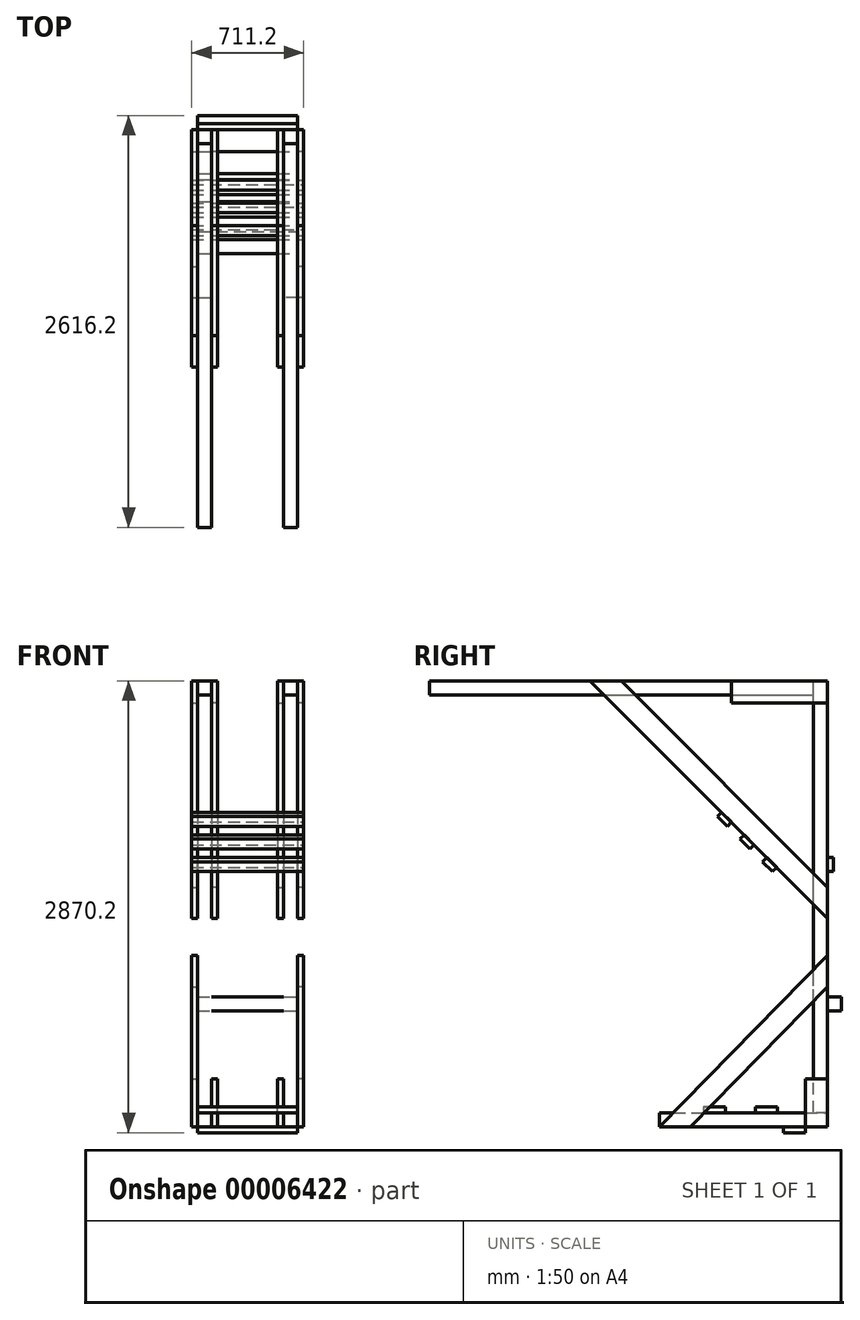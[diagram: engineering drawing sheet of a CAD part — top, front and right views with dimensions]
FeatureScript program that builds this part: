
annotation { "Feature Type Name" : "Feature", "Feature Type Description" : "" }
export const myFeature = defineFeature(function(context is Context, id is Id, definition is map)
    precondition{}
    {
        {
            var Q0;
            Q0=qCreatedBy(makeId("Top.planeOp"),FACE);
            var sketch = newSketch(context, id + "F0", { "sketchPlane" : qUnion([Q0])});
            skLineSegment(sketch, "E0.bottom", {"start": v(-317.5, 0) * mm, "end": v(-228.6, 0) * mm});
            skLineSegment(sketch, "E0.top", {"start": v(-317.5, -88.9) * mm, "end": v(-228.6, -88.9) * mm});
            skLineSegment(sketch, "E0.left", {"start": v(-317.5, 0) * mm, "end": v(-317.5, -88.9) * mm});
            skLineSegment(sketch, "E0.right", {"start": v(-228.6, 0) * mm, "end": v(-228.6, -88.9) * mm});
            skSolve(sketch);
        }
        {
            var Q0;
            Q0 = qSketchRegion(id + "F0", true);
            extrude(context, id + "F1", {"entities" : qUnion([Q0]), "oppositeDirection" : true, "depth" : 2743.2 * mm});
        }
        {
            var Q0;
            Q0=makeQuery(id+"F1.opExtrude","SWEPT_FACE",FACE,{"disambiguationData":[OSD([sQuery(id+"F0.wireOp",EDGE,"E0.bottom")])]});
            var sketch = newSketch(context, id + "F2", { "sketchPlane" : qUnion([Q0])});
            skLineSegment(sketch, "E1.bottom", {"start": v(317.5, -2832.1) * mm, "end": v(228.6, -2832.1) * mm});
            skLineSegment(sketch, "E1.top", {"start": v(317.5, -2743.2) * mm, "end": v(228.6, -2743.2) * mm});
            skLineSegment(sketch, "E1.left", {"start": v(228.6, -2832.1) * mm, "end": v(228.6, -2743.2) * mm});
            skLineSegment(sketch, "E1.right", {"start": v(317.5, -2832.1) * mm, "end": v(317.5, -2743.2) * mm});
            skSolve(sketch);
        }
        {
            var Q0;
            Q0=makeQuery(id+"F2.imprint","IMPRINT",FACE,{"disambiguationData":[TD([[makeQuery(id+"F2.imprint","IMPRINT",EDGE,{"derivedFrom":sQuery(id+"F2.wireOp",EDGE,"E1.bottom")}),-1.0]])]});
            extrude(context, id + "F3", {"entities" : qUnion([Q0]), "oppositeDirection" : true, "depth" : 1066.8 * mm});
        }
        {
            var Q0;
            Q0=makeQuery(id+"F1.opExtrude","SWEPT_FACE",FACE,{"disambiguationData":[OSD([sQuery(id+"F0.wireOp",EDGE,"E0.right")])]});
            var sketch = newSketch(context, id + "F4", { "sketchPlane" : qUnion([Q0])});
            skLineSegment(sketch, "E2.bottom", {"start": v(0, -2832.1) * mm, "end": v(-139.7, -2832.1) * mm});
            skLineSegment(sketch, "E2.top", {"start": v(0, -2527.3) * mm, "end": v(-139.7, -2527.3) * mm});
            skLineSegment(sketch, "E2.left", {"start": v(0, -2832.1) * mm, "end": v(0, -2527.3) * mm});
            skLineSegment(sketch, "E2.right", {"start": v(-139.7, -2832.1) * mm, "end": v(-139.7, -2527.3) * mm});
            skSolve(sketch);
        }
        {
            var Q0;
            {var subQ5=sQuery(id+"F4.wireOp",EDGE,"E2.right");Q0=makeQuery(id+"F4.imprint","IMPRINT",FACE,{"disambiguationData":[TD([[makeQuery(id+"F4.imprint","IMPRINT",EDGE,{"derivedFrom":subQ5}),-1.0]])]});}
            var Q1;
            {var subQ6=sQuery(id+"F4.wireOp",EDGE,"E2.left");Q1=makeQuery(id+"F4.imprint","IMPRINT",FACE,{"disambiguationData":[TD([[makeQuery(id+"F4.imprint","IMPRINT",EDGE,{"derivedFrom":subQ6}),1.0]])]});}
            extrude(context, id + "F5", {"entities" : qUnion([Q0, Q1]), "depth" : 38.1 * mm});
        }
        {
            var Q0;
            Q0=makeQuery(id+"F1.opExtrude","SWEPT_FACE",FACE,{"disambiguationData":[OSD([sQuery(id+"F0.wireOp",EDGE,"E0.top")])]});
            var sketch = newSketch(context, id + "F6", { "sketchPlane" : qUnion([Q0])});
            skLineSegment(sketch, "E3.bottom", {"start": v(-317.5, 0) * mm, "end": v(-228.6, 0) * mm});
            skLineSegment(sketch, "E3.top", {"start": v(-317.5, -88.9) * mm, "end": v(-228.6, -88.9) * mm});
            skLineSegment(sketch, "E3.left", {"start": v(-317.5, 0) * mm, "end": v(-317.5, -88.9) * mm});
            skLineSegment(sketch, "E3.right", {"start": v(-228.6, 0) * mm, "end": v(-228.6, -88.9) * mm});
            skSolve(sketch);
        }
        {
            var Q0;
            Q0=makeQuery(id+"F6.imprint","IMPRINT",FACE,{"disambiguationData":[TD([[makeQuery(id+"F6.imprint","IMPRINT",EDGE,{"derivedFrom":sQuery(id+"F6.wireOp",EDGE,"E3.bottom")}),-1.0]])]});
            extrude(context, id + "F7", {"entities" : qUnion([Q0]), "depth" : 2438.4 * mm});
        }
        {
            var Q0;
            Q0=makeQuery(id+"F1.opExtrude","SWEPT_FACE",FACE,{"disambiguationData":[OSD([sQuery(id+"F0.wireOp",EDGE,"E0.right")])]});
            var sketch = newSketch(context, id + "F8", { "sketchPlane" : qUnion([Q0])});
            skLineSegment(sketch, "E4.bottom", {"start": v(0, 0) * mm, "end": v(-609.6, 0) * mm});
            skLineSegment(sketch, "E4.top", {"start": v(0, -139.7) * mm, "end": v(-609.6, -139.7) * mm});
            skLineSegment(sketch, "E4.left", {"start": v(0, 0) * mm, "end": v(0, -139.7) * mm});
            skLineSegment(sketch, "E4.right", {"start": v(-609.6, 0) * mm, "end": v(-609.6, -139.7) * mm});
            skLineSegment(sketch, "E5.0", {"start": v(-2527.3, -88.9) * mm, "end": v(-88.9, -88.9) * mm, "construction": true});
            skSolve(sketch);
        }
        {
            var Q0;
            {var subQ5=sQuery(id+"F8.wireOp",EDGE,"E4.right");Q0=makeQuery(id+"F8.imprint","IMPRINT",FACE,{"disambiguationData":[TD([[makeQuery(id+"F8.imprint","IMPRINT",EDGE,{"derivedFrom":subQ5}),1.0]])]});}
            var Q1;
            {var subQ6=sQuery(id+"F8.wireOp",EDGE,"E4.left");Q1=makeQuery(id+"F8.imprint","IMPRINT",FACE,{"disambiguationData":[TD([[makeQuery(id+"F8.imprint","IMPRINT",EDGE,{"derivedFrom":subQ6}),1.0]])]});}
            extrude(context, id + "F9", {"entities" : qUnion([Q0, Q1]), "depth" : 38.1 * mm});
        }
        {
            var Q0;
            Q0=makeQuery(id+"F7.opExtrude","SWEPT_FACE",FACE,{"disambiguationData":[OSD([sQuery(id+"F6.wireOp",EDGE,"E3.right")])]});
            var sketch = newSketch(context, id + "F10", { "sketchPlane" : qUnion([Q0])});
            skLineSegment(sketch, "E6.0", {"start": v(0, -2743.2) * mm, "end": v(0, 0) * mm, "construction": true});
            skLineSegment(sketch, "E7", {"start": v(-1508.68, 0) * mm, "end": v(0, -1508.68) * mm});
            skLineSegment(sketch, "E8", {"start": v(0, -1508.68) * mm, "end": v(0, -1311.12) * mm});
            skLineSegment(sketch, "E9", {"start": v(0, -1311.12) * mm, "end": v(-1311.12, 0) * mm});
            skLineSegment(sketch, "E10", {"start": v(-1311.12, 0) * mm, "end": v(-1508.68, 0) * mm});
            skLineSegment(sketch, "E11", {"start": v(-1311.12, 0) * mm, "end": v(0, 0) * mm, "construction": true});
            skLineSegment(sketch, "E12", {"start": v(0, -1311.12) * mm, "end": v(0, 0) * mm, "construction": true});
            skSolve(sketch);
        }
        {
            var Q0;
            Q0=makeQuery(id+"F7.opExtrude","SWEPT_FACE",FACE,{"disambiguationData":[OSD([sQuery(id+"F6.wireOp",EDGE,"E3.right")])]});
            var Q1;
            Q1=makeQuery(id+"F7.opExtrude","SWEPT_FACE",FACE,{"disambiguationData":[OSD([sQuery(id+"F6.wireOp",EDGE,"E3.left")])]});
            cPlane(context, id + "F11", {"entities" : qUnion([Q0, Q1]), "cplaneType" : CPlaneType.MID_PLANE, "offset" : 152.4 * mm, "width" : 152.4 * mm, "height" : 152.4 * mm});
        }
        {
            var Q0;
            {var subQ5=sQuery(id+"F10.wireOp",EDGE,"E8");Q0=makeQuery(id+"F10.imprint","IMPRINT",FACE,{"disambiguationData":[TD([[makeQuery(id+"F10.imprint","IMPRINT",EDGE,{"derivedFrom":subQ5}),1.0]])]});}
            var Q1;
            {var subQ6=sQuery(id+"F10.wireOp",EDGE,"E10");Q1=makeQuery(id+"F10.imprint","IMPRINT",FACE,{"disambiguationData":[TD([[makeQuery(id+"F10.imprint","IMPRINT",EDGE,{"derivedFrom":subQ6}),-1.0]])]});}
            extrude(context, id + "F12", {"entities" : qUnion([Q0, Q1]), "depth" : 38.1 * mm});
        }
        {
            var Q0;
            Q0=makeQuery(id+"F9.opExtrude","SWEPT_BODY",BODY,{"disambiguationData":[OSD([sQuery(id+"F8.wireOp",EDGE,"E4.bottom"),sQuery(id+"F8.wireOp",EDGE,"E4.top"),sQuery(id+"F8.wireOp",EDGE,"E4.left"),sQuery(id+"F8.wireOp",EDGE,"E4.right")])]});
            var Q1;
            Q1=makeQuery(id+"F5.opExtrude","SWEPT_BODY",BODY,{"disambiguationData":[OSD([sQuery(id+"F4.wireOp",EDGE,"E2.bottom"),sQuery(id+"F4.wireOp",EDGE,"E2.top"),sQuery(id+"F4.wireOp",EDGE,"E2.left"),sQuery(id+"F4.wireOp",EDGE,"E2.right")])]});
            var Q2;
            Q2=makeQuery(id+"F12.opExtrude","SWEPT_BODY",BODY,{"disambiguationData":[OSD([sQuery(id+"F10.wireOp",EDGE,"E7"),sQuery(id+"F10.wireOp",EDGE,"E8"),sQuery(id+"F10.wireOp",EDGE,"E9"),sQuery(id+"F10.wireOp",EDGE,"E10")])]});
            var Q3;
            Q3=qCreatedBy(id+"F11.planeOp",FACE);
            mirror(context, id + "F13", {"entities" : qUnion([Q0, Q1, Q2]), "mirrorPlane" : qUnion([Q3])});
        }
        {
            var Q0;
            Q0=makeQuery(id+"F1.opExtrude","SWEPT_FACE",FACE,{"disambiguationData":[OSD([sQuery(id+"F0.wireOp",EDGE,"E0.left")])]});
            var sketch = newSketch(context, id + "F14", { "sketchPlane" : qUnion([Q0])});
            skLineSegment(sketch, "E13.0", {"start": v(1066.8, -2832.1) * mm, "end": v(0, -2832.1) * mm, "construction": true});
            skLineSegment(sketch, "E14", {"start": v(0, -1943.32) * mm, "end": v(871.18, -2832.1) * mm});
            skLineSegment(sketch, "E15", {"start": v(871.18, -2832.1) * mm, "end": v(1066.8, -2832.1) * mm});
            skLineSegment(sketch, "E16", {"start": v(1066.8, -2832.1) * mm, "end": v(0, -1743.75) * mm});
            skLineSegment(sketch, "E17", {"start": v(0, -1743.75) * mm, "end": v(0, -1943.32) * mm});
            skSolve(sketch);
        }
        {
            var Q0;
            {var subQ5=sQuery(id+"F14.wireOp",EDGE,"E15");Q0=makeQuery(id+"F14.imprint","IMPRINT",FACE,{"disambiguationData":[TD([[makeQuery(id+"F14.imprint","IMPRINT",EDGE,{"derivedFrom":subQ5}),1.0]])]});}
            var Q1;
            {var subQ6=sQuery(id+"F14.wireOp",EDGE,"E17");Q1=makeQuery(id+"F14.imprint","IMPRINT",FACE,{"disambiguationData":[TD([[makeQuery(id+"F14.imprint","IMPRINT",EDGE,{"derivedFrom":subQ6}),-1.0]])]});}
            extrude(context, id + "F15", {"entities" : qUnion([Q0, Q1]), "depth" : 38.1 * mm});
        }
        {
            var Q0;
            Q0=makeQuery(id+"F1.opExtrude","SWEPT_BODY",BODY,{"disambiguationData":[OSD([sQuery(id+"F0.wireOp",EDGE,"E0.bottom"),sQuery(id+"F0.wireOp",EDGE,"E0.top"),sQuery(id+"F0.wireOp",EDGE,"E0.left"),sQuery(id+"F0.wireOp",EDGE,"E0.right")])]});
            var Q1;
            Q1=makeQuery(id+"F3.opExtrude","SWEPT_BODY",BODY,{"disambiguationData":[OSD([sQuery(id+"F2.wireOp",EDGE,"E1.bottom"),sQuery(id+"F2.wireOp",EDGE,"E1.top"),sQuery(id+"F2.wireOp",EDGE,"E1.left"),sQuery(id+"F2.wireOp",EDGE,"E1.right")])]});
            var Q2;
            Q2=makeQuery(id+"F5.opExtrude","SWEPT_BODY",BODY,{"disambiguationData":[OSD([sQuery(id+"F4.wireOp",EDGE,"E2.bottom"),sQuery(id+"F4.wireOp",EDGE,"E2.top"),sQuery(id+"F4.wireOp",EDGE,"E2.left"),sQuery(id+"F4.wireOp",EDGE,"E2.right")])]});
            var Q3;
            Q3=makeQuery(id+"F7.opExtrude","SWEPT_BODY",BODY,{"disambiguationData":[OSD([sQuery(id+"F6.wireOp",EDGE,"E3.bottom"),sQuery(id+"F6.wireOp",EDGE,"E3.top"),sQuery(id+"F6.wireOp",EDGE,"E3.left"),sQuery(id+"F6.wireOp",EDGE,"E3.right")])]});
            var Q4;
            Q4=makeQuery(id+"F9.opExtrude","SWEPT_BODY",BODY,{"disambiguationData":[OSD([sQuery(id+"F8.wireOp",EDGE,"E4.bottom"),sQuery(id+"F8.wireOp",EDGE,"E4.top"),sQuery(id+"F8.wireOp",EDGE,"E4.left"),sQuery(id+"F8.wireOp",EDGE,"E4.right")])]});
            var Q5;
            Q5=makeQuery(id+"F13.opPattern","COPY",BODY,{"derivedFrom":makeQuery(id+"F9.opExtrude","SWEPT_BODY",BODY,{"disambiguationData":[OSD([sQuery(id+"F8.wireOp",EDGE,"E4.bottom"),sQuery(id+"F8.wireOp",EDGE,"E4.top"),sQuery(id+"F8.wireOp",EDGE,"E4.left"),sQuery(id+"F8.wireOp",EDGE,"E4.right")])]}),"instanceName":"1"});
            var Q6;
            Q6=makeQuery(id+"F13.opPattern","COPY",BODY,{"derivedFrom":makeQuery(id+"F5.opExtrude","SWEPT_BODY",BODY,{"disambiguationData":[OSD([sQuery(id+"F4.wireOp",EDGE,"E2.bottom"),sQuery(id+"F4.wireOp",EDGE,"E2.top"),sQuery(id+"F4.wireOp",EDGE,"E2.left"),sQuery(id+"F4.wireOp",EDGE,"E2.right")])]}),"instanceName":"1"});
            var Q7;
            Q7=makeQuery(id+"F15.opExtrude","SWEPT_BODY",BODY,{"disambiguationData":[OSD([sQuery(id+"F14.wireOp",EDGE,"E14"),sQuery(id+"F14.wireOp",EDGE,"E15"),sQuery(id+"F14.wireOp",EDGE,"E16"),sQuery(id+"F14.wireOp",EDGE,"E17")])]});
            var Q8;
            Q8=makeQuery(id+"F13.opPattern","COPY",BODY,{"derivedFrom":makeQuery(id+"F12.opExtrude","SWEPT_BODY",BODY,{"disambiguationData":[OSD([sQuery(id+"F10.wireOp",EDGE,"E7"),sQuery(id+"F10.wireOp",EDGE,"E8"),sQuery(id+"F10.wireOp",EDGE,"E9"),sQuery(id+"F10.wireOp",EDGE,"E10")])]}),"instanceName":"1"});
            var Q9;
            Q9=makeQuery(id+"F12.opExtrude","SWEPT_BODY",BODY,{"disambiguationData":[OSD([sQuery(id+"F10.wireOp",EDGE,"E7"),sQuery(id+"F10.wireOp",EDGE,"E8"),sQuery(id+"F10.wireOp",EDGE,"E9"),sQuery(id+"F10.wireOp",EDGE,"E10")])]});
            var Q10;
            Q10=qCreatedBy(makeId("Right.planeOp"),FACE);
            mirror(context, id + "F16", {"entities" : qUnion([Q0, Q1, Q2, Q3, Q4, Q5, Q6, Q7, Q8, Q9]), "mirrorPlane" : qUnion([Q10])});
        }
        {
            var Q0;
            Q0=makeQuery(id+"F3.opExtrude","SWEPT_FACE",FACE,{"disambiguationData":[OSD([sQuery(id+"F2.wireOp",EDGE,"E1.top")])]});
            var sketch = newSketch(context, id + "F17", { "sketchPlane" : qUnion([Q0])});
            skLineSegment(sketch, "E18.bottom", {"start": v(-317.5, -317.5) * mm, "end": v(317.5, -317.5) * mm});
            skLineSegment(sketch, "E18.top", {"start": v(-317.5, -457.2) * mm, "end": v(317.5, -457.2) * mm});
            skLineSegment(sketch, "E18.left", {"start": v(-317.5, -317.5) * mm, "end": v(-317.5, -457.2) * mm});
            skLineSegment(sketch, "E18.right", {"start": v(317.5, -317.5) * mm, "end": v(317.5, -457.2) * mm});
            skLineSegment(sketch, "E19.bottom", {"start": v(-317.5, -647.7) * mm, "end": v(317.5, -647.7) * mm});
            skLineSegment(sketch, "E19.top", {"start": v(-317.5, -787.4) * mm, "end": v(317.5, -787.4) * mm});
            skLineSegment(sketch, "E19.left", {"start": v(-317.5, -647.7) * mm, "end": v(-317.5, -787.4) * mm});
            skLineSegment(sketch, "E19.right", {"start": v(317.5, -647.7) * mm, "end": v(317.5, -787.4) * mm});
            skSolve(sketch);
        }
        {
            var Q0;
            Q0 = qSketchRegion(id + "F17", true);
            extrude(context, id + "F18", {"entities" : qUnion([Q0]), "depth" : 38.1 * mm});
        }
        {
            var Q0;
            Q0=makeQuery(id+"F3.opExtrude","SWEPT_FACE",FACE,{"disambiguationData":[OSD([sQuery(id+"F2.wireOp",EDGE,"E1.bottom")])]});
            var sketch = newSketch(context, id + "F19", { "sketchPlane" : qUnion([Q0])});
            skLineSegment(sketch, "E20.bottom", {"start": v(-317.5, 139.7) * mm, "end": v(317.5, 139.7) * mm});
            skLineSegment(sketch, "E20.top", {"start": v(-317.5, 279.4) * mm, "end": v(317.5, 279.4) * mm});
            skLineSegment(sketch, "E20.left", {"start": v(-317.5, 139.7) * mm, "end": v(-317.5, 279.4) * mm});
            skLineSegment(sketch, "E20.right", {"start": v(317.5, 139.7) * mm, "end": v(317.5, 279.4) * mm});
            skSolve(sketch);
        }
        {
            var Q0;
            Q0 = qSketchRegion(id + "F19", true);
            extrude(context, id + "F20", {"entities" : qUnion([Q0]), "depth" : 38.1 * mm});
        }
        {
            var Q0;
            Q0=makeQuery(id+"F1.opExtrude","SWEPT_FACE",FACE,{"disambiguationData":[OSD([sQuery(id+"F0.wireOp",EDGE,"E0.bottom")])]});
            var sketch = newSketch(context, id + "F21", { "sketchPlane" : qUnion([Q0])});
            skLineSegment(sketch, "E21.bottom", {"start": v(317.5, -2006.6) * mm, "end": v(-317.5, -2006.6) * mm});
            skLineSegment(sketch, "E21.top", {"start": v(317.5, -2095.5) * mm, "end": v(-317.5, -2095.5) * mm});
            skLineSegment(sketch, "E21.left", {"start": v(317.5, -2006.6) * mm, "end": v(317.5, -2095.5) * mm});
            skLineSegment(sketch, "E21.right", {"start": v(-317.5, -2006.6) * mm, "end": v(-317.5, -2095.5) * mm});
            skSolve(sketch);
        }
        {
            var Q0;
            Q0 = qSketchRegion(id + "F21", true);
            extrude(context, id + "F22", {"entities" : qUnion([Q0]), "depth" : 88.9 * mm});
        }
        {
            var Q0;
            Q0=makeQuery(id+"F13.opPattern","COPY",FACE,{"derivedFrom":makeQuery(id+"F12.opExtrude","SWEPT_FACE",FACE,{"disambiguationData":[OSD([sQuery(id+"F10.wireOp",EDGE,"E7")])]}),"instanceName":"1"});
            var sketch = newSketch(context, id + "F23", { "sketchPlane" : qUnion([Q0])});
            skLineSegment(sketch, "E22.bottom", {"start": v(-355.6, -609.6) * mm, "end": v(355.6, -609.6) * mm});
            skLineSegment(sketch, "E22.top", {"start": v(-355.6, -520.7) * mm, "end": v(355.6, -520.7) * mm});
            skLineSegment(sketch, "E22.left", {"start": v(-355.6, -609.6) * mm, "end": v(-355.6, -520.7) * mm});
            skLineSegment(sketch, "E22.right", {"start": v(355.6, -609.6) * mm, "end": v(355.6, -520.7) * mm});
            skLineSegment(sketch, "E23.0.1.0", {"start": v(-355.6, -406.4) * mm, "end": v(355.6, -406.4) * mm});
            skLineSegment(sketch, "E23.0.1.1", {"start": v(-355.6, -317.5) * mm, "end": v(355.6, -317.5) * mm});
            skLineSegment(sketch, "E23.0.1.2", {"start": v(355.6, -406.4) * mm, "end": v(355.6, -317.5) * mm});
            skLineSegment(sketch, "E23.0.1.3", {"start": v(-355.6, -406.4) * mm, "end": v(-355.6, -317.5) * mm});
            skLineSegment(sketch, "E23.0.2.0", {"start": v(-355.6, -203.2) * mm, "end": v(355.6, -203.2) * mm});
            skLineSegment(sketch, "E23.0.2.1", {"start": v(-355.6, -114.3) * mm, "end": v(355.6, -114.3) * mm});
            skLineSegment(sketch, "E23.0.2.2", {"start": v(355.6, -203.2) * mm, "end": v(355.6, -114.3) * mm});
            skLineSegment(sketch, "E23.0.2.3", {"start": v(-355.6, -203.2) * mm, "end": v(-355.6, -114.3) * mm});
            skLineSegment(sketch, "E23.direction1", {"start": v(-355.6, -609.6) * mm, "end": v(-330.2, -609.6) * mm, "construction": true});
            skLineSegment(sketch, "E23.direction2", {"start": v(-355.6, -609.6) * mm, "end": v(-355.6, -406.4) * mm, "construction": true});
            skSolve(sketch);
        }
        {
            var Q0;
            Q0 = qSketchRegion(id + "F23", true);
            extrude(context, id + "F24", {"entities" : qUnion([Q0]), "depth" : 38.1 * mm});
        }
        {
            var Q0;
            Q0=makeQuery(id+"F1.opExtrude","SWEPT_FACE",FACE,{"disambiguationData":[OSD([sQuery(id+"F0.wireOp",EDGE,"E0.bottom")])]});
            var sketch = newSketch(context, id + "F25", { "sketchPlane" : qUnion([Q0])});
            skLineSegment(sketch, "E24.bottom", {"start": v(317.5, -1212.33) * mm, "end": v(-317.5, -1212.33) * mm});
            skLineSegment(sketch, "E24.top", {"start": v(317.5, -1123.43) * mm, "end": v(-317.5, -1123.43) * mm});
            skLineSegment(sketch, "E24.left", {"start": v(317.5, -1212.33) * mm, "end": v(317.5, -1123.43) * mm});
            skLineSegment(sketch, "E24.right", {"start": v(-317.5, -1212.33) * mm, "end": v(-317.5, -1123.43) * mm});
            skSolve(sketch);
        }
        {
            var Q0;
            Q0 = qSketchRegion(id + "F25", true);
            extrude(context, id + "F26", {"entities" : qUnion([Q0]), "depth" : 38.1 * mm});
        }
    });
